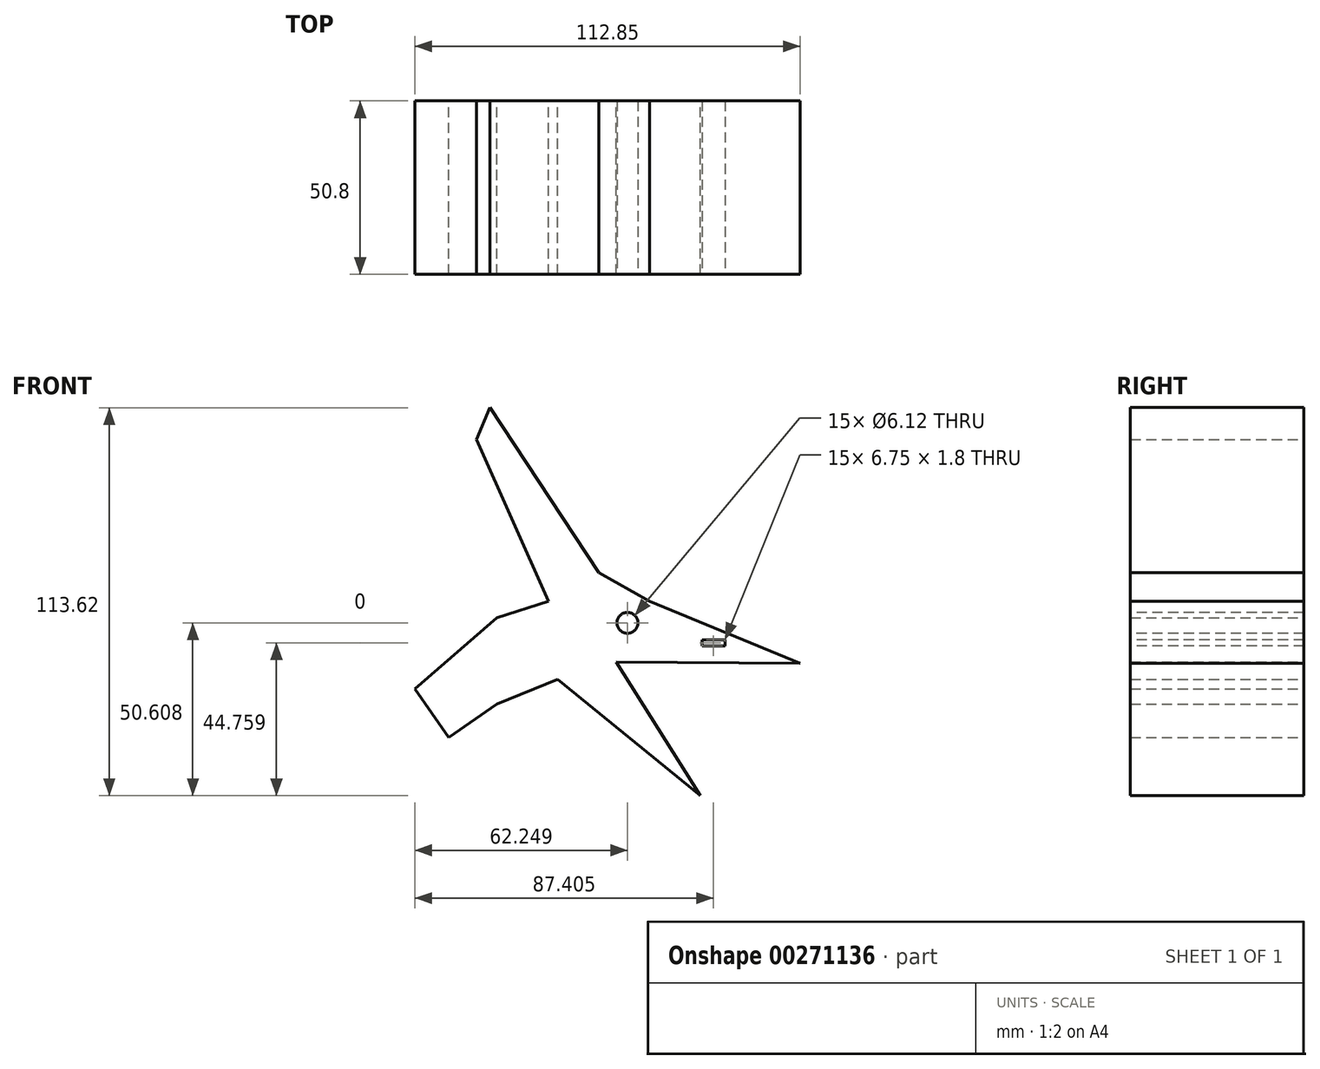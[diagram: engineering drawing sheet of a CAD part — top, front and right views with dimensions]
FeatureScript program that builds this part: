
annotation { "Feature Type Name" : "Feature", "Feature Type Description" : "" }
export const myFeature = defineFeature(function(context is Context, id is Id, definition is map)
    precondition{}
    {
        {
            var Q0;
            Q0=qCreatedBy(makeId("Front.planeOp"),FACE);
            var sketch = newSketch(context, id + "F0", { "sketchPlane" : qUnion([Q0])});
            skLineSegment(sketch, "E0", {"start": v(62.44, 1.72) * mm, "end": v(18.33, 19.86) * mm});
            skLineSegment(sketch, "E1", {"start": v(18.33, 19.86) * mm, "end": v(3.44, 28.26) * mm});
            skLineSegment(sketch, "E2", {"start": v(3.44, 28.26) * mm, "end": v(-28.45, 76.57) * mm});
            skLineSegment(sketch, "E3", {"start": v(-28.45, 76.57) * mm, "end": v(-32.31, 67.19) * mm});
            skLineSegment(sketch, "E4", {"start": v(-32.31, 67.19) * mm, "end": v(-11.27, 19.86) * mm});
            skLineSegment(sketch, "E5", {"start": v(-11.27, 19.86) * mm, "end": v(-26.35, 15.09) * mm});
            skLineSegment(sketch, "E6", {"start": v(-26.35, 15.09) * mm, "end": v(-50.41, -5.73) * mm});
            skLineSegment(sketch, "E7", {"start": v(-50.41, -5.73) * mm, "end": v(-40.48, -20.05) * mm});
            skLineSegment(sketch, "E8", {"start": v(-40.48, -20.05) * mm, "end": v(-26.35, -10.25) * mm});
            skLineSegment(sketch, "E9", {"start": v(-26.35, -10.25) * mm, "end": v(-8.6, -3.06) * mm});
            skLineSegment(sketch, "E10", {"start": v(-8.6, -3.06) * mm, "end": v(33.23, -37.05) * mm});
            skLineSegment(sketch, "E11", {"start": v(33.23, -37.05) * mm, "end": v(8.6, 2.1) * mm});
            skLineSegment(sketch, "E12", {"start": v(8.6, 2.1) * mm, "end": v(62.44, 1.72) * mm});
            skSolve(sketch);
        }
        {
            var Q0;
            Q0 = qSketchRegion(id + "F0", true);
            extrude(context, id + "F1", {"entities" : qUnion([Q0]), "depth" : 50.8 * mm});
        }
        {
            var Q0;
            Q0=makeQuery(id+"F1.opExtrude","CAP_FACE",FACE,{"disambiguationData":[OSD([sQuery(id+"F0.wireOp",EDGE,"E0"),sQuery(id+"F0.wireOp",EDGE,"E1"),sQuery(id+"F0.wireOp",EDGE,"E2"),sQuery(id+"F0.wireOp",EDGE,"E3"),sQuery(id+"F0.wireOp",EDGE,"E4"),sQuery(id+"F0.wireOp",EDGE,"E5"),sQuery(id+"F0.wireOp",EDGE,"E6"),sQuery(id+"F0.wireOp",EDGE,"E7"),sQuery(id+"F0.wireOp",EDGE,"E8"),sQuery(id+"F0.wireOp",EDGE,"E9"),sQuery(id+"F0.wireOp",EDGE,"E10"),sQuery(id+"F0.wireOp",EDGE,"E11"),sQuery(id+"F0.wireOp",EDGE,"E12")])],"isStart":false});
            var sketch = newSketch(context, id + "F2", { "sketchPlane" : qUnion([Q0])});
            skCircle(sketch, "E13", {"center": v(11.84, 13.56) * mm, "radius": 3.06 * mm});
            skSolve(sketch);
        }
        {
            var Q0;
            Q0 = qSketchRegion(id + "F2", true);
            extrude(context, id + "F3", {"entities" : qUnion([Q0]), "operationType" : NewBodyOperationType.REMOVE, "oppositeDirection" : true, "depth" : 50.8 * mm});
        }
        {
            var Q0;
            Q0=makeQuery(id+"F1.opExtrude","CAP_FACE",FACE,{"disambiguationData":[OSD([sQuery(id+"F0.wireOp",EDGE,"E0"),sQuery(id+"F0.wireOp",EDGE,"E1"),sQuery(id+"F0.wireOp",EDGE,"E2"),sQuery(id+"F0.wireOp",EDGE,"E3"),sQuery(id+"F0.wireOp",EDGE,"E4"),sQuery(id+"F0.wireOp",EDGE,"E5"),sQuery(id+"F0.wireOp",EDGE,"E6"),sQuery(id+"F0.wireOp",EDGE,"E7"),sQuery(id+"F0.wireOp",EDGE,"E8"),sQuery(id+"F0.wireOp",EDGE,"E9"),sQuery(id+"F0.wireOp",EDGE,"E10"),sQuery(id+"F0.wireOp",EDGE,"E11"),sQuery(id+"F0.wireOp",EDGE,"E12")])],"isStart":false});
            var sketch = newSketch(context, id + "F4", { "sketchPlane" : qUnion([Q0])});
            skLineSegment(sketch, "E14.bottom", {"start": v(33.62, 8.6) * mm, "end": v(40.37, 8.6) * mm});
            skLineSegment(sketch, "E14.top", {"start": v(33.62, 6.81) * mm, "end": v(40.37, 6.81) * mm});
            skLineSegment(sketch, "E14.left", {"start": v(33.62, 8.6) * mm, "end": v(33.62, 6.81) * mm});
            skLineSegment(sketch, "E14.right", {"start": v(40.37, 8.6) * mm, "end": v(40.37, 6.81) * mm});
            skSolve(sketch);
        }
        {
            var Q0;
            Q0 = qSketchRegion(id + "F4", true);
            extrude(context, id + "F5", {"entities" : qUnion([Q0]), "operationType" : NewBodyOperationType.REMOVE, "oppositeDirection" : true, "depth" : 50.8 * mm});
        }
    });
